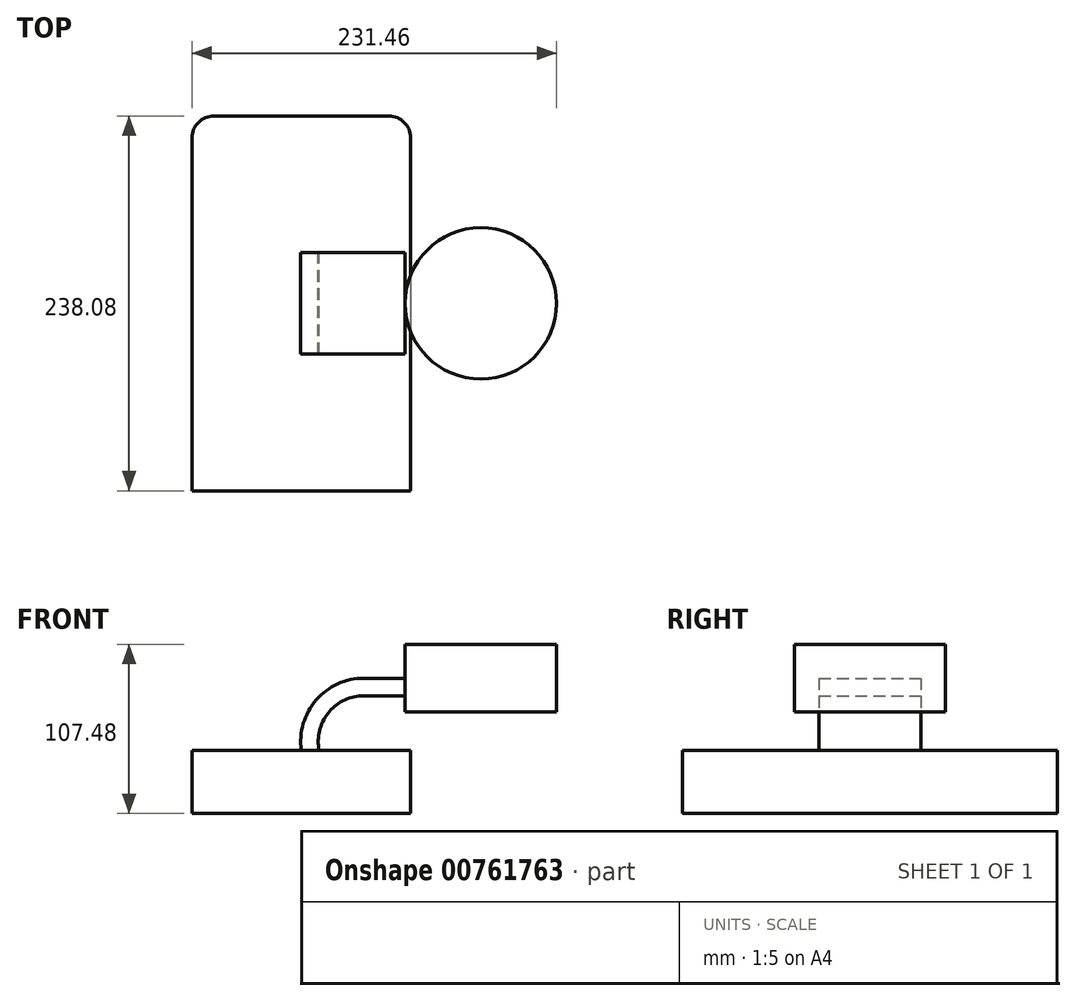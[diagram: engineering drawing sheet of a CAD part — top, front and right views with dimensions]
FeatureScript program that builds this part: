
annotation { "Feature Type Name" : "Feature", "Feature Type Description" : "" }
export const myFeature = defineFeature(function(context is Context, id is Id, definition is map)
    precondition{}
    {
        {
            var Q0;
            Q0=qCreatedBy(makeId("Front.planeOp"),FACE);
            var sketch = newSketch(context, id + "F0", { "sketchPlane" : qUnion([Q0])});
            skLineSegment(sketch, "E0.bottom", {"start": v(69.4, 20.05) * mm, "end": v(-69.4, 20.05) * mm});
            skLineSegment(sketch, "E0.top", {"start": v(69.4, -20.05) * mm, "end": v(-69.4, -20.05) * mm});
            skLineSegment(sketch, "E0.left", {"start": v(69.4, 20.05) * mm, "end": v(69.4, -20.05) * mm});
            skLineSegment(sketch, "E0.right", {"start": v(-69.4, 20.05) * mm, "end": v(-69.4, -20.05) * mm});
            skPoint(sketch, "E0.middle", {"position": v(0, 0) * mm});
            skLineSegment(sketch, "E1.bottom", {"start": v(162.06, 87.43) * mm, "end": v(65.9, 87.43) * mm});
            skLineSegment(sketch, "E1.top", {"start": v(162.06, 44.36) * mm, "end": v(65.9, 44.36) * mm});
            skLineSegment(sketch, "E1.left", {"start": v(162.06, 87.43) * mm, "end": v(162.06, 44.36) * mm});
            skLineSegment(sketch, "E1.right", {"start": v(65.9, 87.43) * mm, "end": v(65.9, 44.36) * mm});
            skPoint(sketch, "E1.middle", {"position": v(113.98, 65.9) * mm});
            skLineSegment(sketch, "E2", {"start": v(65.9, 65.9) * mm, "end": v(39.73, 65.9) * mm});
            skArc(sketch, "E3", {"start": v(39.73, 65.9) * mm, "mid": v(9.4, 52.04) * mm, "end": v(0, 20.05) * mm});
            skArc(sketch, "E4.0", {"start": v(39.73, 54.77) * mm, "mid": v(17.8, 44.76) * mm, "end": v(11.01, 21.63) * mm});
            skLineSegment(sketch, "E4.1", {"start": v(77.6, 54.77) * mm, "end": v(39.73, 54.77) * mm});
            skLineSegment(sketch, "E5", {"start": v(11.01, 21.63) * mm, "end": v(11.24, 20.05) * mm});
            skLineSegment(sketch, "E6", {"start": v(113.98, 87.43) * mm, "end": v(113.98, 44.36) * mm});
            skSolve(sketch);
        }
        {
            var Q0;
            Q0=makeQuery(id+"F0.imprint","IMPRINT",FACE,{"disambiguationData":[TD([[makeQuery(id+"F0.imprint","IMPRINT",EDGE,{"derivedFrom":sQuery(id+"F0.wireOp",EDGE,"E0.top")}),-1.0]])]});
            extrude(context, id + "F1", {"entities" : qUnion([Q0]), "endBound" : BoundingType.SYMMETRIC, "oppositeDirection" : true, "depth" : 238.08 * mm, "offsetDistance" : 25.4 * mm});
        }
        {
            var Q0;
            {var subQ1=sQuery(id+"F0.wireOp",EDGE,"E2");Q0=makeQuery(id+"F0.imprint","IMPRINT",FACE,{"disambiguationData":[TD([[makeQuery(id+"F0.imprint","IMPRINT",EDGE,{"derivedFrom":subQ1}),1.0]])]});}
            extrude(context, id + "F2", {"entities" : qUnion([Q0]), "operationType" : NewBodyOperationType.ADD, "endBound" : BoundingType.SYMMETRIC, "depth" : 64.6 * mm, "offsetDistance" : 25.4 * mm});
        }
        {
            var Q0;
            {var subQ0=sQuery(id+"F0.wireOp",EDGE,"E1.left");Q0=makeQuery(id+"F0.imprint","IMPRINT",FACE,{"disambiguationData":[TD([[makeQuery(id+"F0.imprint","IMPRINT",EDGE,{"derivedFrom":subQ0}),-1.0]])]});}
            var Q1;
            Q1=sQuery(id+"F0.wireOp",EDGE,"E6");
            revolve(context, id + "F3", {"operationType" : NewBodyOperationType.ADD, "surfaceOperationType" : NewSurfaceOperationType.NEW, "entities" : qUnion([Q0]), "axis" : qUnion([Q1]), "revolveType" : RevolveType.FULL});
        }
        {
            var Q0;
            Q0=makeQuery(id+"F1.opExtrude","CAP_EDGE",EDGE,{"disambiguationData":[OSD([sQuery(id+"F0.wireOp",EDGE,"E0.right")])],"isStart":false});
            var Q1;
            Q1=makeQuery(id+"F1.opExtrude","CAP_EDGE",EDGE,{"disambiguationData":[OSD([sQuery(id+"F0.wireOp",EDGE,"E0.left")])],"isStart":false});
            fillet(context, id + "F4", {"entities" : qUnion([Q0, Q1]), "radius" : 13.8 * mm, "tangentPropagation" : true, "allowEdgeOverflow" : false});
        }
    });
